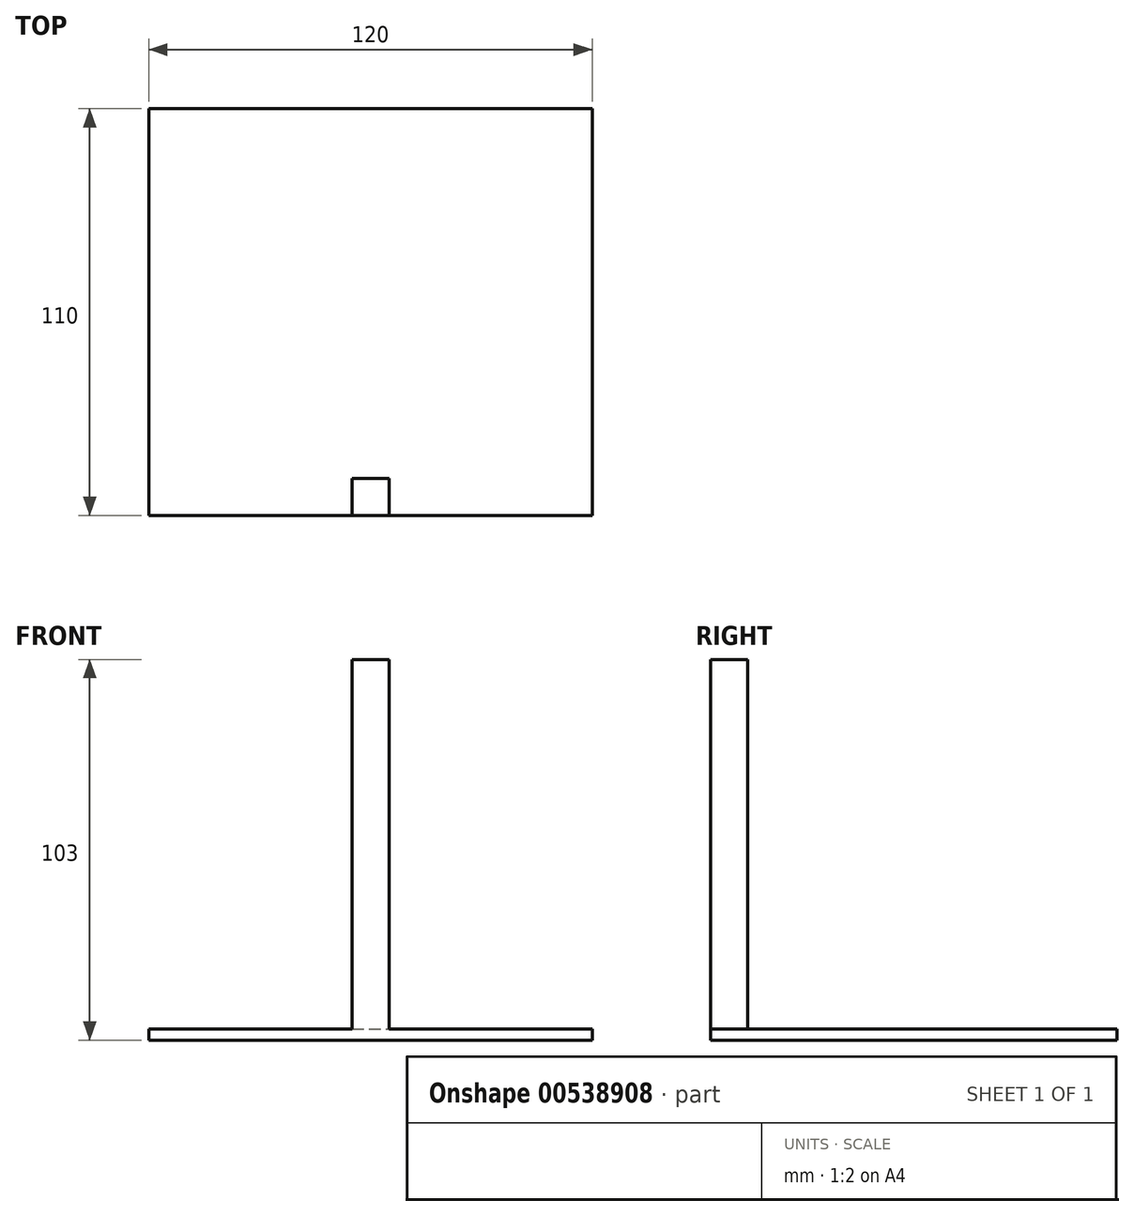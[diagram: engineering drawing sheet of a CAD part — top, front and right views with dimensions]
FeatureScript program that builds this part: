
annotation { "Feature Type Name" : "Feature", "Feature Type Description" : "" }
export const myFeature = defineFeature(function(context is Context, id is Id, definition is map)
    precondition{}
    {
        {
            var Q0;
            Q0=qCreatedBy(makeId("Front.planeOp"),FACE);
            var sketch = newSketch(context, id + "F0", { "sketchPlane" : qUnion([Q0])});
            skLineSegment(sketch, "E0.bottom", {"start": v(-6.56, 82) * mm, "end": v(3.44, 82) * mm});
            skLineSegment(sketch, "E0.top", {"start": v(-6.56, -18) * mm, "end": v(3.44, -18) * mm});
            skLineSegment(sketch, "E0.left", {"start": v(-6.56, 82) * mm, "end": v(-6.56, -18) * mm});
            skLineSegment(sketch, "E0.right", {"start": v(3.44, 82) * mm, "end": v(3.44, -18) * mm});
            skSolve(sketch);
        }
        {
            var Q0;
            Q0 = qSketchRegion(id + "F0", true);
            extrude(context, id + "F1", {"entities" : qUnion([Q0]), "depth" : 10 * mm, "offsetDistance" : 25 * mm});
        }
        {
            var Q0;
            Q0=makeQuery(id+"F1.opExtrude","CAP_FACE",FACE,{"disambiguationData":[OSD([sQuery(id+"F0.wireOp",EDGE,"E0.bottom"),sQuery(id+"F0.wireOp",EDGE,"E0.top"),sQuery(id+"F0.wireOp",EDGE,"E0.left"),sQuery(id+"F0.wireOp",EDGE,"E0.right")])],"isStart":false});
            var sketch = newSketch(context, id + "F2", { "sketchPlane" : qUnion([Q0])});
            skLineSegment(sketch, "E1", {"start": v(-6.56, -18) * mm, "end": v(-61.56, -18) * mm});
            skLineSegment(sketch, "E2", {"start": v(-61.56, -18) * mm, "end": v(-61.56, -21) * mm});
            skLineSegment(sketch, "E3", {"start": v(-61.56, -21) * mm, "end": v(58.44, -21) * mm});
            skLineSegment(sketch, "E4", {"start": v(58.44, -21) * mm, "end": v(58.44, -18) * mm});
            skLineSegment(sketch, "E5", {"start": v(58.44, -18) * mm, "end": v(3.44, -18) * mm});
            skLineSegment(sketch, "E6", {"start": v(-6.56, -18) * mm, "end": v(3.44, -18) * mm});
            skSolve(sketch);
        }
        {
            var Q0;
            Q0=makeQuery(id+"F2.imprint","IMPRINT",FACE,{"disambiguationData":[TD([[makeQuery(id+"F2.imprint","IMPRINT",EDGE,{"derivedFrom":sQuery(id+"F2.wireOp",EDGE,"E1")}),1.0]])]});
            extrude(context, id + "F3", {"entities" : qUnion([Q0]), "operationType" : NewBodyOperationType.ADD, "oppositeDirection" : true, "depth" : 110 * mm, "offsetDistance" : 25 * mm});
        }
        {
            var Q0;
            Q0=makeQuery(id+"F1.opExtrude","SWEPT_FACE",FACE,{"disambiguationData":[OSD([sQuery(id+"F0.wireOp",EDGE,"E0.right")])]});
            cPlane(context, id + "F4", {"entities" : qUnion([Q0]), "cplaneType" : CPlaneType.OFFSET, "offset" : 1 * mm, "width" : 150 * mm, "height" : 150 * mm});
        }
    });
